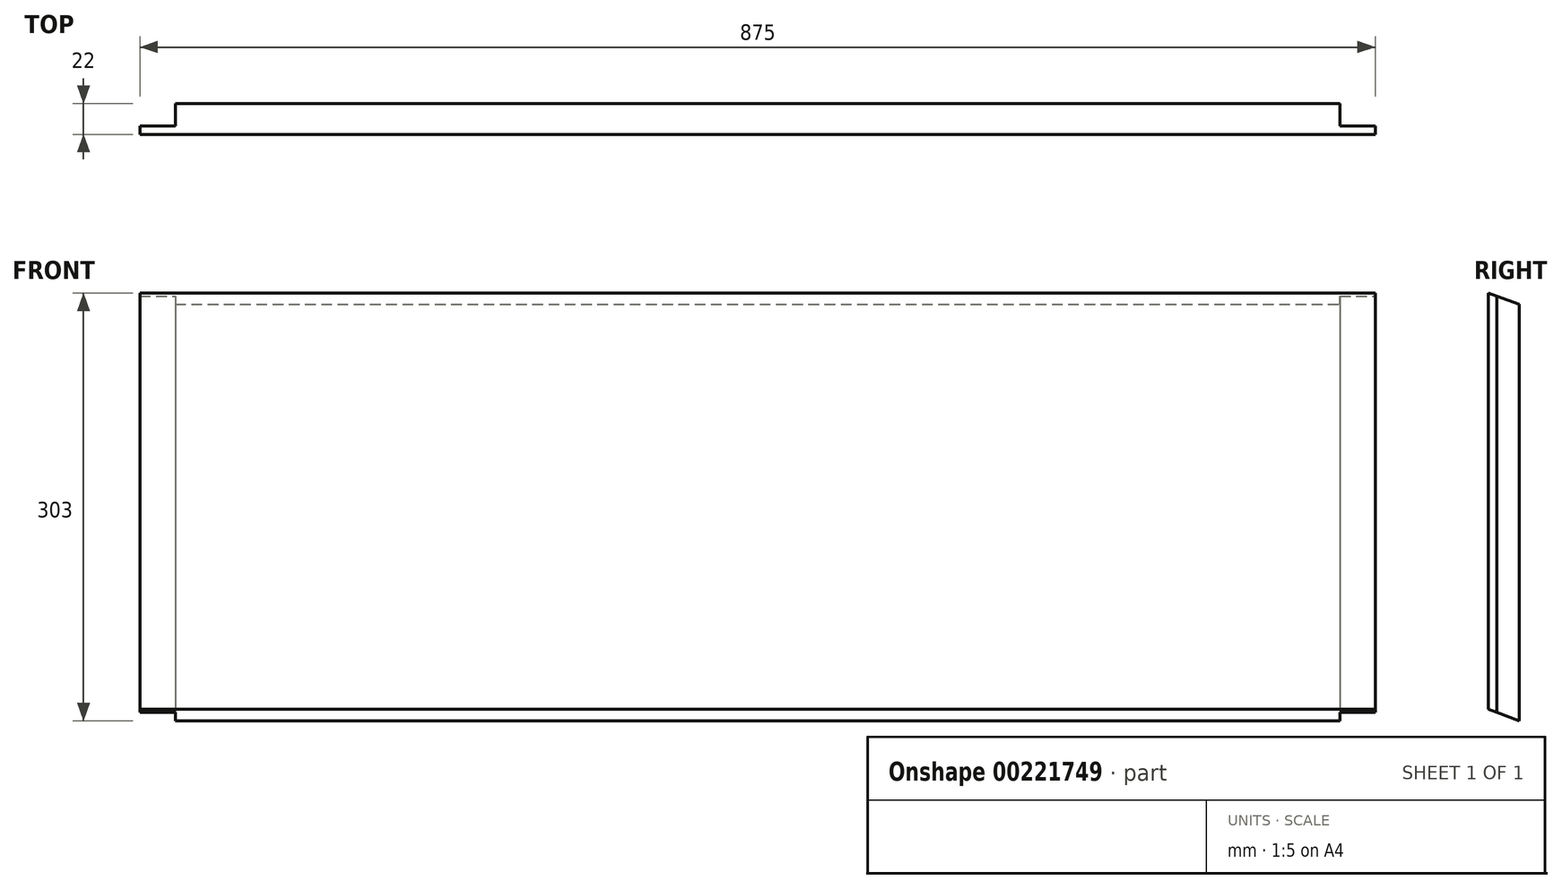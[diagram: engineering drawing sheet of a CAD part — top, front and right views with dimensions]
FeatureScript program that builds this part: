
annotation { "Feature Type Name" : "Feature", "Feature Type Description" : "" }
export const myFeature = defineFeature(function(context is Context, id is Id, definition is map)
    precondition{}
    {
        {
            var Q0;
            Q0=qCreatedBy(makeId("Front.planeOp"),FACE);
            var sketch = newSketch(context, id + "F0", { "sketchPlane" : qUnion([Q0])});
            skLineSegment(sketch, "E0.bottom", {"start": v(-437.5, 151.5) * mm, "end": v(437.5, 151.5) * mm});
            skLineSegment(sketch, "E0.top", {"start": v(-437.5, -151.5) * mm, "end": v(437.5, -151.5) * mm});
            skLineSegment(sketch, "E0.left", {"start": v(-437.5, 151.5) * mm, "end": v(-437.5, -151.5) * mm});
            skLineSegment(sketch, "E0.right", {"start": v(437.5, 151.5) * mm, "end": v(437.5, -151.5) * mm});
            skPoint(sketch, "E0.middle", {"position": v(0, 0) * mm});
            skLineSegment(sketch, "E1", {"start": v(0, 0) * mm, "end": v(0, -151.5) * mm, "construction": true});
            skSolve(sketch);
        }
        {
            var Q0;
            Q0 = qSketchRegion(id + "F0", true);
            extrude(context, id + "F1", {"entities" : qUnion([Q0]), "depth" : 22 * mm});
        }
        {
            var Q0;
            Q0=makeQuery(id+"F1.opExtrude","CAP_EDGE",EDGE,{"disambiguationData":[OSD([sQuery(id+"F0.wireOp",EDGE,"E0.top")])],"isStart":false});
            var Q1;
            Q1=makeQuery(id+"F1.opExtrude","CAP_EDGE",EDGE,{"disambiguationData":[OSD([sQuery(id+"F0.wireOp",EDGE,"E0.bottom")])],"isStart":true});
            chamfer(context, id + "F2", {"entities" : qUnion([Q0, Q1]), "chamferType" : ChamferType.OFFSET_ANGLE, "width" : 22 * mm, "oppositeDirection" : true, "angle" : 20 * degree, "tangentPropagation" : true});
        }
        {
            var Q0;
            Q0=qCreatedBy(makeId("Top.planeOp"),FACE);
            var sketch = newSketch(context, id + "F3", { "sketchPlane" : qUnion([Q0])});
            skLineSegment(sketch, "E2.0", {"start": v(-437.5, 0) * mm, "end": v(437.5, 0) * mm});
            skLineSegment(sketch, "E3.0", {"start": v(437.5, 0) * mm, "end": v(437.5, -22) * mm});
            skLineSegment(sketch, "E4.0", {"start": v(-437.5, -22) * mm, "end": v(-437.5, 0) * mm});
            skLineSegment(sketch, "E5", {"start": v(-412.5, 0) * mm, "end": v(-412.5, -16) * mm});
            skLineSegment(sketch, "E6", {"start": v(-412.5, -16) * mm, "end": v(-437.5, -16) * mm});
            skPoint(sketch, "E6.endSnap0", {"position": v(-437.5, -11) * mm});
            skLineSegment(sketch, "E7", {"start": v(437.5, -16) * mm, "end": v(412.5, -16) * mm});
            skLineSegment(sketch, "E8", {"start": v(412.5, -16) * mm, "end": v(412.5, 0) * mm});
            skSolve(sketch);
        }
        {
            var Q0;
            Q0 = qSketchRegion(id + "F3", true);
            var Q1;
            Q1=makeQuery(id+"F2.opChamfer","BLEND_FACE",FACE,{"disambiguationData":[OSD([sQuery(id+"F0.wireOp",EDGE,"E0.bottom")])]});
            extrude(context, id + "F4", {"entities" : qUnion([Q0]), "operationType" : NewBodyOperationType.REMOVE, "endBound" : BoundingType.SYMMETRIC, "endBoundEntityFace" : qUnion([Q1]), "depth" : 400 * mm});
        }
    });
